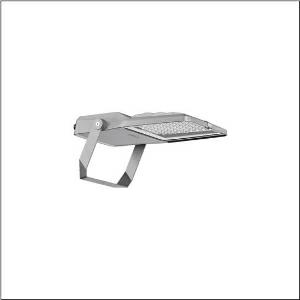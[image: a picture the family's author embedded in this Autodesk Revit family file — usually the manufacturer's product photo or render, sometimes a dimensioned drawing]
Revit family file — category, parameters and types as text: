
# Revit family: floodlight_fl_21_iq_mini___pl43_5xa7772c5a1a_be68
name_source: partatom
category: Lighting Fixtures
units: mm (PartAtom-declared; Revit-internal decimal feet)

## family parameters
Cut with Voids When Loaded = No
Host = Face
Light Source = No
Part Type = Normal
Room Calculation Point = No
Round Connector Dimension = Use Diameter
Shared = No

## types (1)
- --- (1 x LED, 11690 lm, 87.2 W, 4000K)
    Apparent Load = 87 VA
    CIE Flux Codes = 27 78 99 100 100
    Color Rendering = 80
    Color Temperature = 4000K
    Default Elevation = 1800 mm
    Description = Floodlight FL 21 iQ mini, floodlight, primary light control with lens, of PMMA, primary optical cover: protective disc, of toughened safety glass, transparent, light distribution: PL43, light emission: direct distribution, installation type: surface-mounted, LED, High Power LED, rated luminous flux: 11.690lm, luminous efficacy: 134lm/W, light colour: 840, colour temperature: 4000K, control gear: iQ Street-Remote/DALI, control: Street-Remote, Auto-Match, Temp-Guard, Night-Set, Smart-Wire, Desk-Remote (wireless, voltage-free reading and setting of iQ features in the workshop via application-optimized NFC function/RFID function), optimised constant luminous flux control (CLO 2.0), with terminal, 6-pole, mains connection: 220..240V, AC, 50/60Hz, start of lifetime: 87W, end of service life: 92W, reduction: 40W, luminaire housing, of diecast aluminium, powder-coated, Siteco® metallic grey (DB 702S), corrosivity category C5 mid according to DIN EN ISO 12944, suitable for swimming pools, chlorine-resistant, sealing non-destructively replaceable, mounting bracket, of steel, galvanised, powder-coated, Siteco® metallic grey (DB 702S), protection rating (complete): IP66, insulation class (complete): insulation class II (safety insulation), certification: CE, ENEC, VDE, protection symbol: D, impact resistance: IK08, permissible operating ambient temperature: -40..+40°C, permissible operating ambient temperature for outdoor applications: -40..+50°C, standard: DIN EN 12944, LABS conformity tested according to VDMA 24364:2018-05, packaging unit: 1 piece

Light Distribution: PL43
    Height = 70 mm
    Lamp = 1 x LED
    Lamp Light Flux = 11690 lm
    Lamp Power = 87.2 W
    Lamp count = 1
    Length = 485 mm
    Luminous efficacy = 134 lm/W
    Manufacturer = Siteco
    ModVariant = No
    Model = 5XA7772C5A1A
    Number of Poles = 1
    OnlyDefault = Yes
    Power Factor = 1
    Product Name = Floodlight FL 21 iQ mini | PL43
    Product group = floodlight | pylon annexe
    ProductGroupID = 6200
    Protection Class = Protection class II
    Protection Degree = IP 66
    RLX_Detail_Level = 1
    RLX_Emergency_Light_Flux = 0 lm
    RLX_Emergency_Type = 0
    RLX_Emergency_Type_DB = No
    RlxData = <blob elided: 96217 chars, md5=da00a03a>
    Socket = socket
    Standby Power = 0 W
    System Light Flux = 11690 lm
    System Power = 87 W
    Type Comments = factory setting: luminous flux: 100 % | dim-lin: 254 | 456 mA
    Type Image = l_1006845.jpg
    URL = http://relux.com
    VarID = @adj_162126
    Voltage = 0 V
    Weight = 0.00 kg
    Width = 337 mm

## geometry (parser evidence)
native form markers: Blend x4, Sweep x11
no freeform markers — native parametric forms only
